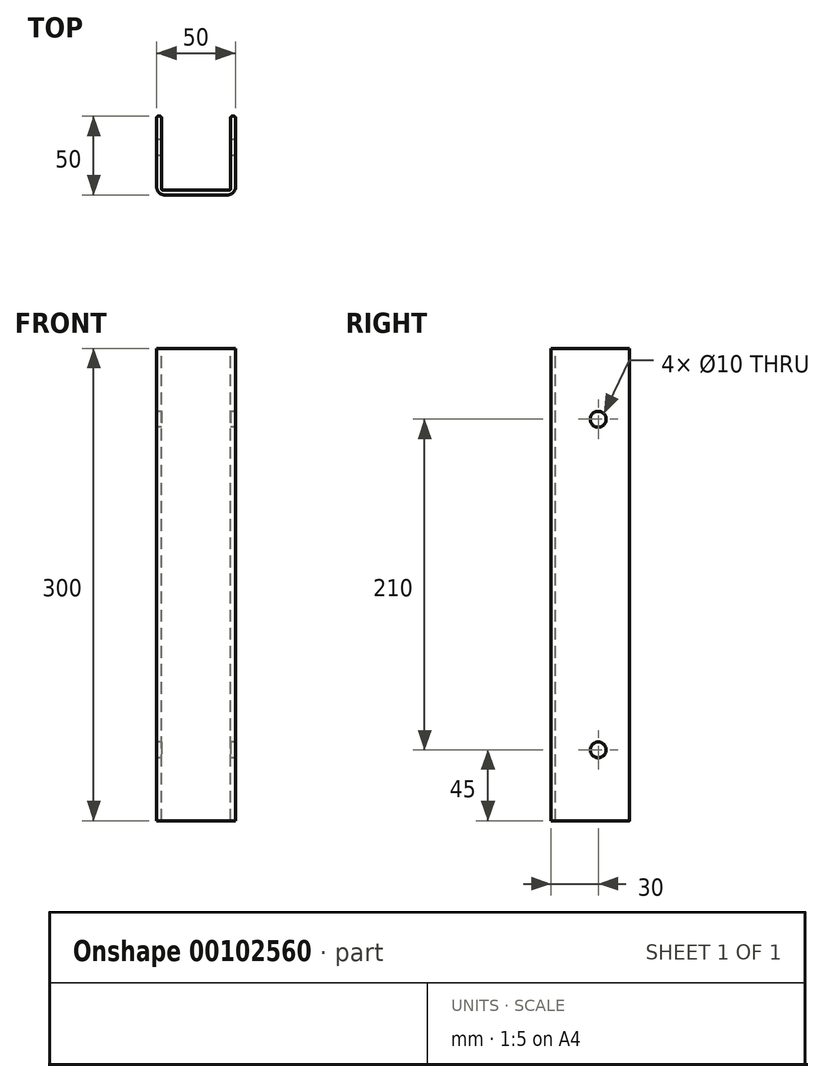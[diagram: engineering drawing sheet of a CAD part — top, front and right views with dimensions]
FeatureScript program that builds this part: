
annotation { "Feature Type Name" : "Feature", "Feature Type Description" : "" }
export const myFeature = defineFeature(function(context is Context, id is Id, definition is map)
    precondition{}
    {
        {
            var Q0;
            Q0=qCreatedBy(makeId("Front.planeOp"),FACE);
            var sketch = newSketch(context, id + "F0", { "sketchPlane" : qUnion([Q0])});
            skLineSegment(sketch, "E0.bottom", {"start": v(0, 0) * mm, "end": v(50, 0) * mm});
            skLineSegment(sketch, "E0.top", {"start": v(0, 300) * mm, "end": v(50, 300) * mm});
            skLineSegment(sketch, "E0.left", {"start": v(0, 0) * mm, "end": v(0, 300) * mm});
            skLineSegment(sketch, "E0.right", {"start": v(50, 0) * mm, "end": v(50, 300) * mm});
            skSolve(sketch);
        }
        {
            var Q0;
            Q0 = qSketchRegion(id + "F0", true);
            extrude(context, id + "F1", {"entities" : qUnion([Q0]), "depth" : 50 * mm, "offsetDistance" : 25 * mm});
        }
        {
            var Q0;
            Q0=makeQuery(id+"F1.opExtrude","SWEPT_FACE",FACE,{"disambiguationData":[OSD([sQuery(id+"F0.wireOp",EDGE,"E0.bottom")])]});
            var Q1;
            Q1=makeQuery(id+"F1.opExtrude","CAP_FACE",FACE,{"disambiguationData":[OSD([sQuery(id+"F0.wireOp",EDGE,"E0.bottom"),sQuery(id+"F0.wireOp",EDGE,"E0.top"),sQuery(id+"F0.wireOp",EDGE,"E0.left"),sQuery(id+"F0.wireOp",EDGE,"E0.right")])],"isStart":true});
            var Q2;
            Q2=makeQuery(id+"F1.opExtrude","SWEPT_FACE",FACE,{"disambiguationData":[OSD([sQuery(id+"F0.wireOp",EDGE,"E0.top")])]});
            shell(context, id + "F2", {"entities" : qUnion([Q0, Q1, Q2]), "thickness" : 3 * mm});
        }
        {
            var Q0;
            Q0=makeQuery(id+"F1.opExtrude","CAP_EDGE",EDGE,{"disambiguationData":[OSD([sQuery(id+"F0.wireOp",EDGE,"E0.right")])],"isStart":false});
            var Q1;
            Q1=makeQuery(id+"F1.opExtrude","CAP_EDGE",EDGE,{"disambiguationData":[OSD([sQuery(id+"F0.wireOp",EDGE,"E0.left")])],"isStart":false});
            fillet(context, id + "F3", {"entities" : qUnion([Q0, Q1]), "tangentPropagation" : true, "radius" : 5 * mm, "defaultsChanged" : false, "vertexSettings" : [], "allowEdgeOverflow" : false});
        }
        {
            var Q0;
            {var subQ0=sQuery(id+"F0.wireOp",EDGE,"E0.right");Q0=makeQuery(id+"F2.opShell","OFFSET_EDGE",EDGE,{"disambiguationData":[OSD([subQ0]),TDD([makeQuery(id+"F1.opExtrude","CAP_EDGE",EDGE,{"disambiguationData":[OSD([subQ0])],"isStart":true})])]});}
            var Q1;
            Q1=makeQuery(id+"F1.opExtrude","CAP_EDGE",EDGE,{"disambiguationData":[OSD([sQuery(id+"F0.wireOp",EDGE,"E0.right")])],"isStart":true});
            var Q2;
            {var subQ0=sQuery(id+"F0.wireOp",EDGE,"E0.left");Q2=makeQuery(id+"F2.opShell","OFFSET_EDGE",EDGE,{"disambiguationData":[OSD([subQ0]),TDD([makeQuery(id+"F1.opExtrude","CAP_EDGE",EDGE,{"disambiguationData":[OSD([subQ0])],"isStart":true})])]});}
            var Q3;
            Q3=makeQuery(id+"F1.opExtrude","CAP_EDGE",EDGE,{"disambiguationData":[OSD([sQuery(id+"F0.wireOp",EDGE,"E0.left")])],"isStart":true});
            var Q4;
            {var subQ0=sQuery(id+"F0.wireOp",EDGE,"E0.left");Q4=makeQuery(id+"F2.opShell","OFFSET_EDGE",EDGE,{"disambiguationData":[OSD([subQ0]),TDD([makeQuery(id+"F1.opExtrude","CAP_EDGE",EDGE,{"disambiguationData":[OSD([subQ0])],"isStart":false})])]});}
            var Q5;
            {var subQ0=sQuery(id+"F0.wireOp",EDGE,"E0.right");Q5=makeQuery(id+"F2.opShell","OFFSET_EDGE",EDGE,{"disambiguationData":[OSD([subQ0]),TDD([makeQuery(id+"F1.opExtrude","CAP_EDGE",EDGE,{"disambiguationData":[OSD([subQ0])],"isStart":false})])]});}
            fillet(context, id + "F4", {"entities" : qUnion([Q0, Q1, Q2, Q3, Q4, Q5]), "tangentPropagation" : true, "radius" : 1 * mm, "defaultsChanged" : false, "vertexSettings" : [], "allowEdgeOverflow" : false});
        }
        {
            var Q0;
            Q0=makeQuery(id+"F1.opExtrude","SWEPT_FACE",FACE,{"disambiguationData":[OSD([sQuery(id+"F0.wireOp",EDGE,"E0.left")])]});
            var sketch = newSketch(context, id + "F5", { "sketchPlane" : qUnion([Q0])});
            skLineSegment(sketch, "E1", {"start": v(20, 300) * mm, "end": v(20, 0) * mm, "construction": true});
            skCircle(sketch, "E2", {"center": v(20, 255) * mm, "radius": 5 * mm});
            skLineSegment(sketch, "E3", {"start": v(1, 150) * mm, "end": v(45, 150) * mm, "construction": true});
            skCircle(sketch, "E4.MirrorC", {"center": v(20, 45) * mm, "radius": 5 * mm});
            skSolve(sketch);
        }
        {
            var Q0;
            Q0 = qSketchRegion(id + "F5", true);
            extrude(context, id + "F6", {"entities" : qUnion([Q0]), "operationType" : NewBodyOperationType.REMOVE, "endBound" : BoundingType.THROUGH_ALL, "oppositeDirection" : true, "depth" : 25 * mm, "offsetDistance" : 25 * mm});
        }
    });
